# Revit family: GRAS_HW-25W-KP-20-30+ROP
name_source: partatom
category: Osprzęt hydrauliczny
revit_build: Autodesk Revit 2018 (Build: 20190510_1515(x64)
units: mm (PartAtom-declared; Revit-internal decimal feet)

## family parameters
Obiekt nadrzędny = Powierzchnia
Punkt obliczania pomieszczeń = Nie
Tnij formami wycięć po wczytaniu = Nie
Typ części = Normalny
Współdzielony = Nie
Wymiar okrągłego złącza = Użyj średnicy

## types (2) — shared parameters
Cabinet_Depth = 250 mm  [stored 0.82021 ft]
Cabinet_Height = 970 mm  [stored 3.18241 ft]
Cabinet_Width = 700 mm  [stored 2.29659 ft]
D1 = 100 mm  [stored 0.328084 ft]
DN = 25 mm  [stored 0.082021 ft]
Flow = 60.0 L/s
H1 = 100 mm  [stored 0.328084 ft]
Hole_Depth = 260 mm
Hole_Height = 990 mm
Hole_Width = 720 mm
K_factor = 42
Opis = https://gras.pl
Producent = GRAS PPPH
URL = http://www.gras.pl
W1 = 100 mm  [stored 0.328084 ft]
zero-valued in all types: 0, Domyślna rzędna

## per-type parameters (varying)
| type | Cabinet_Material |
| HW-25W-KP-20/30 + ROP, RAL9010 | DC01, RAL9010 |
| HW-25W-KP-20/30 + ROP, RAL3000 | DC01, RAL3000 |

note: column(s) folded — value = type name in every type: Model

note: [stored X ft] marks values corroborated as IEEE doubles in the binary element streams (Revit-internal decimal feet)

## geometry (parser evidence)
native form markers: Blend x4
no freeform markers — native parametric forms only
